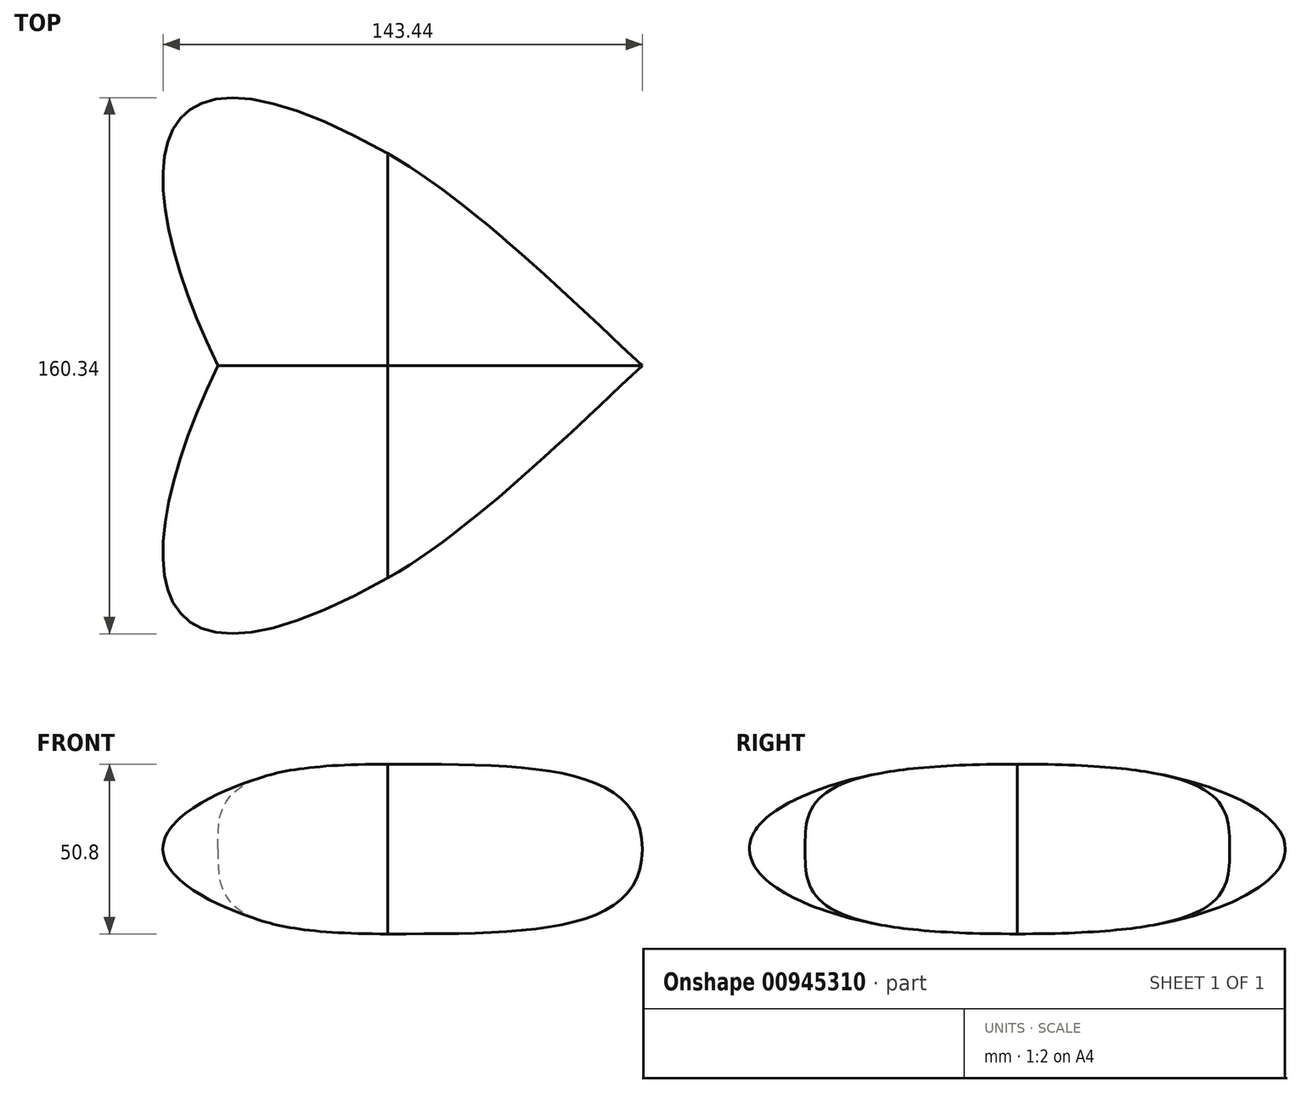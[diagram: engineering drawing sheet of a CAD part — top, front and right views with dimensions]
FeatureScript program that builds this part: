
annotation { "Feature Type Name" : "Feature", "Feature Type Description" : "" }
export const myFeature = defineFeature(function(context is Context, id is Id, definition is map)
    precondition{}
    {
        {
            var Q0;
            Q0=qCreatedBy(makeId("Front.planeOp"),FACE);
            var sketch = newSketch(context, id + "F0", { "sketchPlane" : qUnion([Q0])});
            skLineSegment(sketch, "E0", {"start": v(0, 0) * mm, "end": v(0, 25.4) * mm});
            skLineSegment(sketch, "E1", {"start": v(0, 0) * mm, "end": v(-50.8, 0) * mm});
            skFitSpline(sketch, "E2", {"points": [v(-50.8, 0) * mm, v(0, 25.4) * mm], "startDerivative": vector(0, 43.78) * mm, "endDerivative": vector(152.4, 0) * mm});
            skSolve(sketch);
        }
        {
            var Q0;
            Q0=qCreatedBy(makeId("Front.planeOp"),FACE);
            var sketch = newSketch(context, id + "F1", { "sketchPlane" : qUnion([Q0])});
            skLineSegment(sketch, "E3.0", {"start": v(0, 0) * mm, "end": v(0, 25.4) * mm});
            skLineSegment(sketch, "E4", {"start": v(0, 0) * mm, "end": v(76.2, 0) * mm});
            skFitSpline(sketch, "E5", {"points": [v(0, 25.4) * mm, v(76.2, 0) * mm], "startDerivative": vector(127.08, 0) * mm, "endDerivative": vector(0, -76.2) * mm});
            skSolve(sketch);
        }
        {
            var Q0;
            Q0=qCreatedBy(makeId("Right.planeOp"),FACE);
            var sketch = newSketch(context, id + "F2", { "sketchPlane" : qUnion([Q0])});
            skLineSegment(sketch, "E6.0", {"start": v(0, 0) * mm, "end": v(0, 25.4) * mm});
            skLineSegment(sketch, "E7", {"start": v(0, 0) * mm, "end": v(-63.5, 0) * mm});
            skFitSpline(sketch, "E8", {"points": [v(-63.5, 0) * mm, v(0, 25.4) * mm], "startDerivative": vector(0, 41.8) * mm, "endDerivative": vector(190.5, 0) * mm});
            skSolve(sketch);
        }
        {
            var Q0;
            Q0=qCreatedBy(makeId("Top.planeOp"),FACE);
            var sketch = newSketch(context, id + "F3", { "sketchPlane" : qUnion([Q0])});
            skPoint(sketch, "E9.0", {"position": v(-50.8, 0) * mm});
            skPoint(sketch, "E10.0", {"position": v(0, -63.5) * mm});
            skFitSpline(sketch, "E11", {"points": [v(-50.8, 0) * mm, v(0, -63.5) * mm], "startDerivative": vector(-79, -163.58) * mm, "endDerivative": vector(238.3, 134.35) * mm});
            skLineSegment(sketch, "E12", {"start": v(0, -63.5) * mm, "end": v(-79.43, -108.28) * mm, "construction": true});
            skSolve(sketch);
        }
        {
            var Q0;
            Q0=qCreatedBy(makeId("Top.planeOp"),FACE);
            var sketch = newSketch(context, id + "F4", { "sketchPlane" : qUnion([Q0])});
            skPoint(sketch, "E13.0", {"position": v(0, -63.5) * mm});
            skPoint(sketch, "E14.0", {"position": v(76.2, 0) * mm});
            skLineSegment(sketch, "E15.0", {"start": v(0, -63.5) * mm, "end": v(-79.43, -108.28) * mm, "construction": true});
            skFitSpline(sketch, "E16", {"points": [v(0, -63.5) * mm, v(76.2, 0) * mm], "startDerivative": vector(73.01, 41.17) * mm, "endDerivative": vector(71.18, 66.16) * mm});
            skLineSegment(sketch, "E17", {"start": v(0, -63.5) * mm, "end": v(24.34, -49.78) * mm, "construction": true});
            skSolve(sketch);
        }
        {
            var Q0;
            Q0=makeQuery(id+"F0.imprint","IMPRINT",FACE,{"disambiguationData":[TD([[makeQuery(id+"F0.imprint","IMPRINT",EDGE,{"derivedFrom":sQuery(id+"F0.wireOp",EDGE,"E0")}),1.0]])]});
            var Q1;
            Q1=makeQuery(id+"F2.imprint","IMPRINT",FACE,{"disambiguationData":[TD([[makeQuery(id+"F2.imprint","IMPRINT",EDGE,{"derivedFrom":sQuery(id+"F2.wireOp",EDGE,"E6.0")}),1.0]])]});
            var Q2;
            Q2=sQuery(id+"F3.wireOp",EDGE,"E11");
            loft(context, id + "F5", {"addGuides" : true, "sheetProfilesArray" : [{ "sheetProfileEntities" : qUnion([Q0]) }, { "sheetProfileEntities" : qUnion([Q1]) }], "guidesArray" : [{ "guideEntities" : qUnion([Q2]), "guideDerivativeType" : LoftGuideDerivativeType.DEFAULT, "guideDerivativeMagnitude" : 1 }]});
        }
        {
            var Q1;
            Q1=makeQuery(id+"F5.opLoft","CAP_FACE",FACE,{"disambiguationData":[OSD([makeQuery(id+"F2.imprint","IMPRINT",FACE,{"disambiguationData":[TD([[makeQuery(id+"F2.imprint","IMPRINT",EDGE,{"derivedFrom":sQuery(id+"F2.wireOp",EDGE,"E6.0")}),1.0]])]})])],"isStart":true});
            var Q2;
            Q2=makeQuery(id+"F1.imprint","IMPRINT",FACE,{"disambiguationData":[TD([[makeQuery(id+"F1.imprint","IMPRINT",EDGE,{"derivedFrom":sQuery(id+"F1.wireOp",EDGE,"E3.0")}),-1.0]])]});
            var Q3;
            Q3=sQuery(id+"F4.wireOp",EDGE,"E16");
            loft(context, id + "F6", {"operationType" : NewBodyOperationType.ADD, "addGuides" : true, "sheetProfilesArray" : [{ "sheetProfileEntities" : qUnion([Q1]) }, { "sheetProfileEntities" : qUnion([Q2]) }], "guidesArray" : [{ "guideEntities" : qUnion([Q3]), "guideDerivativeType" : LoftGuideDerivativeType.DEFAULT, "guideDerivativeMagnitude" : 1 }]});
        }
        {
            var Q0;
            Q0=makeQuery(id+"F5.opLoft","SWEPT_BODY",BODY,{"disambiguationData":[OSD([makeQuery(id+"F0.imprint","IMPRINT",FACE,{"disambiguationData":[TD([[makeQuery(id+"F0.imprint","IMPRINT",EDGE,{"derivedFrom":sQuery(id+"F0.wireOp",EDGE,"E0")}),1.0]])]}),makeQuery(id+"F2.imprint","IMPRINT",FACE,{"disambiguationData":[TD([[makeQuery(id+"F2.imprint","IMPRINT",EDGE,{"derivedFrom":sQuery(id+"F2.wireOp",EDGE,"E6.0")}),1.0]])]}),sQuery(id+"F3.wireOp",EDGE,"E11")])]});
            var Q1;
            Q1=makeQuery(id+"F0.imprint","IMPRINT",FACE,{"disambiguationData":[TD([[makeQuery(id+"F0.imprint","IMPRINT",EDGE,{"derivedFrom":sQuery(id+"F0.wireOp",EDGE,"E0")}),1.0]])]});
            mirror(context, id + "F7", {"operationType" : NewBodyOperationType.ADD, "entities" : qUnion([Q0]), "mirrorPlane" : qUnion([Q1])});
        }
        {
            var Q0;
            Q0=makeQuery(id+"F5.opLoft","SWEPT_BODY",BODY,{"disambiguationData":[OSD([makeQuery(id+"F0.imprint","IMPRINT",FACE,{"disambiguationData":[TD([[makeQuery(id+"F0.imprint","IMPRINT",EDGE,{"derivedFrom":sQuery(id+"F0.wireOp",EDGE,"E0")}),1.0]])]}),makeQuery(id+"F2.imprint","IMPRINT",FACE,{"disambiguationData":[TD([[makeQuery(id+"F2.imprint","IMPRINT",EDGE,{"derivedFrom":sQuery(id+"F2.wireOp",EDGE,"E6.0")}),1.0]])]}),sQuery(id+"F3.wireOp",EDGE,"E11")])]});
            var Q1;
            {var subQ0=sQuery(id+"F3.wireOp",EDGE,"E11");var subQ1=sQuery(id+"F2.wireOp",EDGE,"E7");var subQ2=sQuery(id+"F2.wireOp",EDGE,"E6.0");var subQ3=makeQuery(id+"F6.boolean.opBoolean","MERGE",FACE,{"derivedFrom":[makeQuery(id+"F5.opLoft","SWEPT_FACE",FACE,{"disambiguationData":[OSD([sQuery(id+"F0.wireOp",EDGE,"E0"),sQuery(id+"F0.wireOp",EDGE,"E1"),subQ2,subQ1,subQ0])]}),makeQuery(id+"F6.opLoft","SWEPT_FACE",FACE,{"disambiguationData":[OSD([sQuery(id+"F1.wireOp",EDGE,"E3.0"),sQuery(id+"F1.wireOp",EDGE,"E4"),sQuery(id+"F1.wireOp",EDGE,"E5"),subQ2,subQ1,subQ0,sQuery(id+"F4.wireOp",EDGE,"E16")])]})]});Q1=makeQuery(id+"F7.boolean.opBoolean","MERGE",FACE,{"derivedFrom":[subQ3,makeQuery(id+"F7.opPattern","COPY",FACE,{"derivedFrom":subQ3,"instanceName":"1"})]});}
            mirror(context, id + "F8", {"operationType" : NewBodyOperationType.ADD, "entities" : qUnion([Q0]), "mirrorPlane" : qUnion([Q1])});
        }
    });
